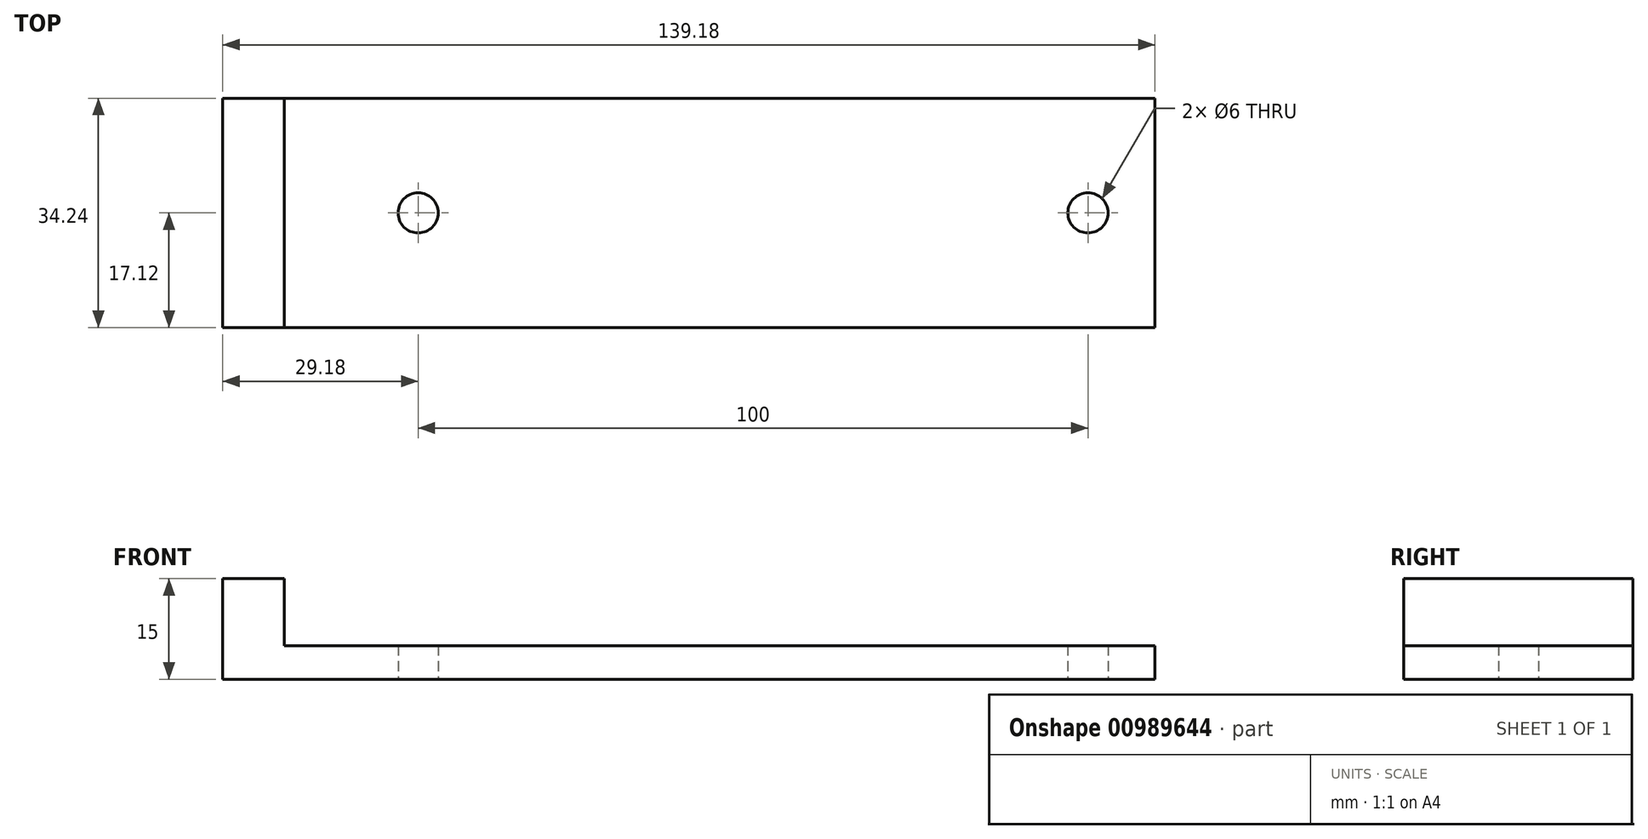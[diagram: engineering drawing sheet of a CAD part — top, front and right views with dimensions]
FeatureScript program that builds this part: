
annotation { "Feature Type Name" : "Feature", "Feature Type Description" : "" }
export const myFeature = defineFeature(function(context is Context, id is Id, definition is map)
    precondition{}
    {
        {
            var Q0;
            Q0=qCreatedBy(makeId("Top.planeOp"),FACE);
            var sketch = newSketch(context, id + "F0", { "sketchPlane" : qUnion([Q0])});
            skLineSegment(sketch, "E0.bottom", {"start": v(-65, -17.12) * mm, "end": v(65, -17.12) * mm});
            skLineSegment(sketch, "E0.top", {"start": v(-65, 17.12) * mm, "end": v(65, 17.12) * mm});
            skLineSegment(sketch, "E0.left", {"start": v(-65, -17.12) * mm, "end": v(-65, 17.12) * mm});
            skLineSegment(sketch, "E0.right", {"start": v(65, -17.12) * mm, "end": v(65, 17.12) * mm});
            skPoint(sketch, "E0.middle", {"position": v(0, 0) * mm});
            skCircle(sketch, "E1", {"center": v(-45, 0) * mm, "radius": 3 * mm});
            skCircle(sketch, "E2", {"center": v(55, 0) * mm, "radius": 3 * mm});
            skLineSegment(sketch, "E3.bottom", {"start": v(-65, 17.12) * mm, "end": v(-74.18, 17.12) * mm});
            skLineSegment(sketch, "E3.top", {"start": v(-65, -17.12) * mm, "end": v(-74.18, -17.12) * mm});
            skLineSegment(sketch, "E3.left", {"start": v(-65, 17.12) * mm, "end": v(-65, -17.12) * mm});
            skLineSegment(sketch, "E3.right", {"start": v(-74.18, 17.12) * mm, "end": v(-74.18, -17.12) * mm});
            skSolve(sketch);
        }
        {
            var Q0;
            Q0=makeQuery(id+"F0.imprint","IMPRINT",FACE,{"disambiguationData":[TD([[makeQuery(id+"F0.imprint","IMPRINT",EDGE,{"derivedFrom":sQuery(id+"F0.wireOp",EDGE,"E0.bottom")}),1.0]])]});
            extrude(context, id + "F1", {"entities" : qUnion([Q0]), "depth" : 5 * mm, "offsetDistance" : 25 * mm});
        }
        {
            var Q0;
            Q0=makeQuery(id+"F0.imprint","IMPRINT",FACE,{"disambiguationData":[TD([[makeQuery(id+"F0.imprint","IMPRINT",EDGE,{"derivedFrom":sQuery(id+"F0.wireOp",EDGE,"E3.bottom")}),1.0]])]});
            extrude(context, id + "F2", {"entities" : qUnion([Q0]), "operationType" : NewBodyOperationType.ADD, "depth" : 15 * mm, "offsetDistance" : 25 * mm});
        }
    });
